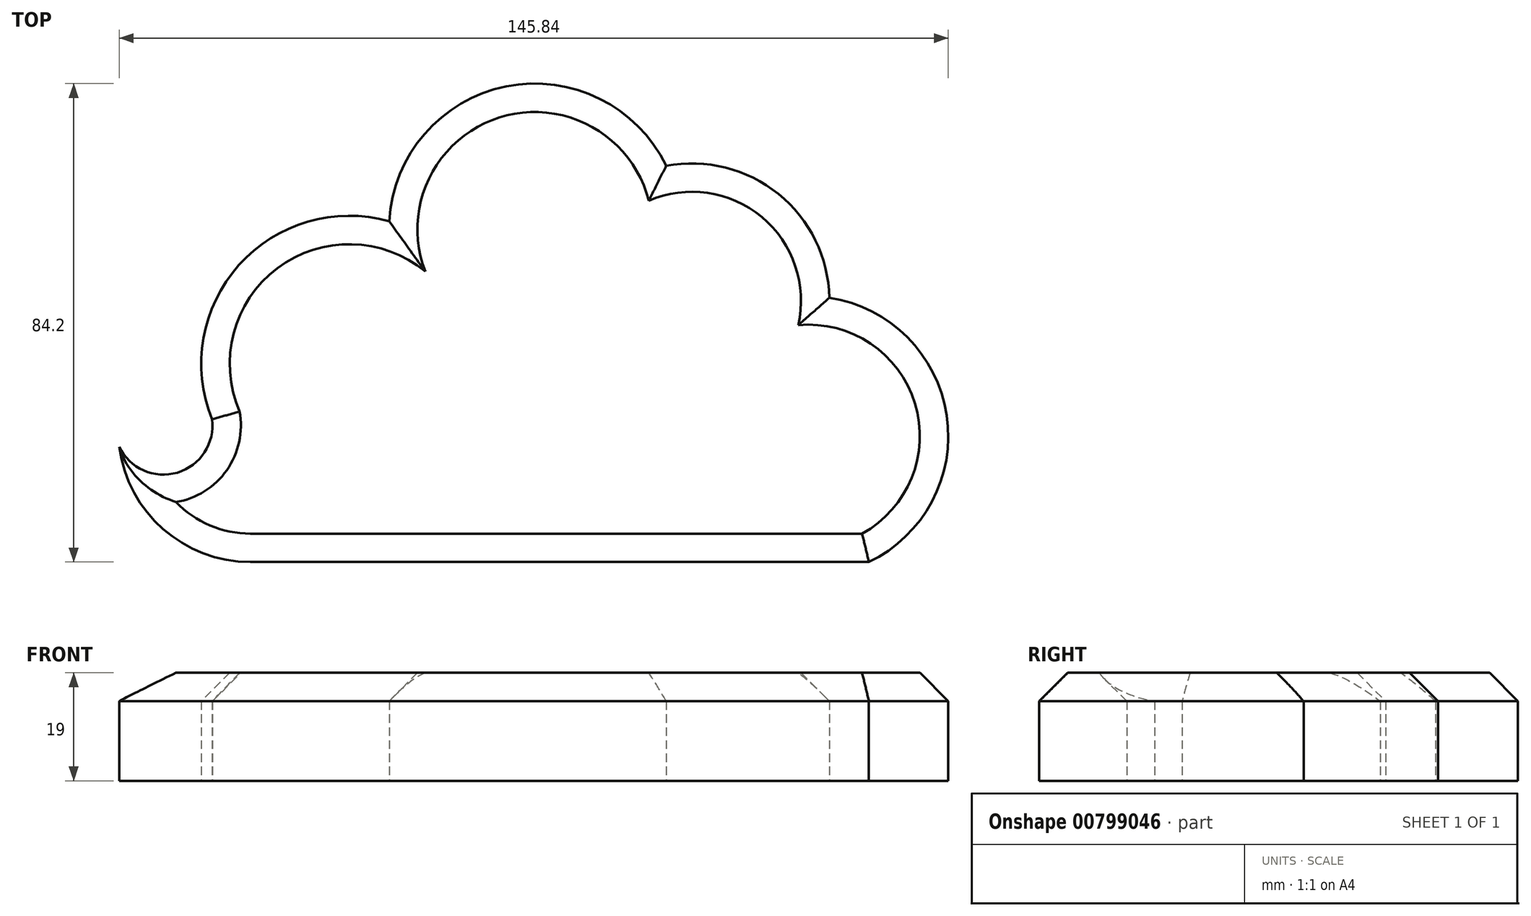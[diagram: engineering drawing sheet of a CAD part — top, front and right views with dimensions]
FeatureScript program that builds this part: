
annotation { "Feature Type Name" : "Feature", "Feature Type Description" : "" }
export const myFeature = defineFeature(function(context is Context, id is Id, definition is map)
    precondition{}
    {
        {
            var Q0;
            Q0=qCreatedBy(makeId("Top.planeOp"),FACE);
            var sketch = newSketch(context, id + "F0", { "sketchPlane" : qUnion([Q0])});
            skArc(sketch, "E0", {"start": v(52.12, 32) * mm, "mid": v(39.52, 52.71) * mm, "end": v(15.28, 52.06) * mm});
            skArc(sketch, "E1", {"start": v(23.4, 55.22) * mm, "mid": v(-4.72, 69.2) * mm, "end": v(-25.3, 45.47) * mm});
            skArc(sketch, "E2", {"start": v(-25.3, 45.47) * mm, "mid": v(-51.74, 37.77) * mm, "end": v(-56.46, 10.64) * mm});
            skArc(sketch, "E3", {"start": v(59.07, -14.5) * mm, "mid": v(72.77, 11.32) * mm, "end": v(52.12, 32) * mm});
            skLineSegment(sketch, "E4", {"start": v(59.07, -14.5) * mm, "end": v(-49.7, -14.5) * mm});
            skArc(sketch, "E5", {"start": v(-72.8, 5.8) * mm, "mid": v(-65.07, -8.7) * mm, "end": v(-49.7, -14.5) * mm});
            skArc(sketch, "E6", {"start": v(-72.8, 5.8) * mm, "mid": v(-62.56, 1.24) * mm, "end": v(-56.46, 10.64) * mm});
            skLineSegment(sketch, "E7", {"start": v(-56.46, 10.64) * mm, "end": v(0.53, 10.64) * mm});
            skLineSegment(sketch, "E8", {"start": v(-51.74, 37.77) * mm, "end": v(-0.22, 37.77) * mm});
            skLineSegment(sketch, "E9", {"start": v(-0.22, 37.77) * mm, "end": v(51.3, 37.77) * mm});
            skLineSegment(sketch, "E10", {"start": v(0.53, 10.64) * mm, "end": v(72.86, 10.64) * mm});
            skSolve(sketch);
        }
        {
            var Q0;
            {var subQ0=sQuery(id+"F0.wireOp",EDGE,"E4");Q0=makeQuery(id+"F0.imprint","IMPRINT",FACE,{"disambiguationData":[TD([[makeQuery(id+"F0.imprint","IMPRINT",EDGE,{"derivedFrom":subQ0}),-1.0]])]});}
            extrude(context, id + "F1", {"entities" : qUnion([Q0]), "depth" : 19 * mm, "offsetDistance" : 25 * mm});
        }
        {
            var Q0;
            {var subQ3=sQuery(id+"F0.wireOp",EDGE,"E7");Q0=makeQuery(id+"F0.imprint","IMPRINT",FACE,{"disambiguationData":[TD([[makeQuery(id+"F0.imprint","IMPRINT",EDGE,{"derivedFrom":subQ3}),1.0]])]});}
            extrude(context, id + "F2", {"entities" : qUnion([Q0]), "operationType" : NewBodyOperationType.ADD, "depth" : 19 * mm, "offsetDistance" : 25 * mm});
        }
        {
            var Q0;
            {var subQ1=sQuery(id+"F0.wireOp",EDGE,"E1");Q0=makeQuery(id+"F0.imprint","IMPRINT",FACE,{"disambiguationData":[TD([[makeQuery(id+"F0.imprint","IMPRINT",EDGE,{"derivedFrom":subQ1}),1.0]])]});}
            extrude(context, id + "F3", {"entities" : qUnion([Q0]), "operationType" : NewBodyOperationType.ADD, "depth" : 19 * mm, "offsetDistance" : 25 * mm});
        }
        {
            var Q0;
            Q0=makeQuery(id+"F1.opExtrude","CAP_EDGE",EDGE,{"disambiguationData":[OSD([sQuery(id+"F0.wireOp",EDGE,"E6")])],"isStart":false});
            var Q1;
            Q1=makeQuery(id+"F1.opExtrude","CAP_EDGE",EDGE,{"disambiguationData":[OSD([sQuery(id+"F0.wireOp",EDGE,"E5")])],"isStart":false});
            var Q2;
            Q2=makeQuery(id+"F1.opExtrude","CAP_EDGE",EDGE,{"disambiguationData":[OSD([sQuery(id+"F0.wireOp",EDGE,"E4")])],"isStart":false});
            var Q3;
            {var subQ0=sQuery(id+"F0.wireOp",EDGE,"E3");Q3=makeQuery(id+"F2.boolean.opBoolean","MERGE",EDGE,{"derivedFrom":[makeQuery(id+"F1.opExtrude","CAP_EDGE",EDGE,{"disambiguationData":[OSD([subQ0])],"isStart":false}),makeQuery(id+"F2.opExtrude","CAP_EDGE",EDGE,{"disambiguationData":[OSD([subQ0])],"isStart":false})]});}
            var Q4;
            {var subQ0=sQuery(id+"F0.wireOp",EDGE,"E0");Q4=makeQuery(id+"F3.boolean.opBoolean","MERGE",EDGE,{"derivedFrom":[makeQuery(id+"F2.opExtrude","CAP_EDGE",EDGE,{"disambiguationData":[OSD([subQ0])],"isStart":false}),makeQuery(id+"F3.opExtrude","CAP_EDGE",EDGE,{"disambiguationData":[OSD([subQ0])],"isStart":false})]});}
            var Q5;
            Q5=makeQuery(id+"F3.opExtrude","CAP_EDGE",EDGE,{"disambiguationData":[OSD([sQuery(id+"F0.wireOp",EDGE,"E1")])],"isStart":false});
            var Q6;
            {var subQ0=sQuery(id+"F0.wireOp",EDGE,"E9");var subQ1=sQuery(id+"F0.wireOp",EDGE,"E8");var subQ2=sQuery(id+"F0.wireOp",EDGE,"E2");var subQ3=sQuery(id+"F0.wireOp",EDGE,"E0");var subQ4=sQuery(id+"F0.wireOp",EDGE,"E10");var subQ5=sQuery(id+"F0.wireOp",EDGE,"E7");var subQ6=sQuery(id+"F0.wireOp",EDGE,"E3");Q6=makeQuery(id+"F3.boolean.opBoolean","MERGE",FACE,{"derivedFrom":[makeQuery(id+"F2.boolean.opBoolean","MERGE",FACE,{"derivedFrom":[makeQuery(id+"F1.opExtrude","CAP_FACE",FACE,{"disambiguationData":[OSD([subQ6,sQuery(id+"F0.wireOp",EDGE,"E4"),sQuery(id+"F0.wireOp",EDGE,"E5"),sQuery(id+"F0.wireOp",EDGE,"E6"),subQ5,subQ4])],"isStart":false}),makeQuery(id+"F2.opExtrude","CAP_FACE",FACE,{"disambiguationData":[OSD([subQ3,subQ2,subQ6,subQ5,subQ1,subQ0,subQ4])],"isStart":false})]}),makeQuery(id+"F3.opExtrude","CAP_FACE",FACE,{"disambiguationData":[OSD([subQ3,sQuery(id+"F0.wireOp",EDGE,"E1"),subQ2,subQ1,subQ0])],"isStart":false})]});}
            chamfer(context, id + "F4", {"entities" : qUnion([Q0, Q1, Q2, Q3, Q4, Q5, Q6]), "width" : 5 * mm, "tangentPropagation" : true});
        }
    });
